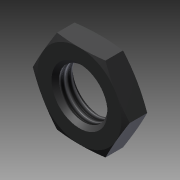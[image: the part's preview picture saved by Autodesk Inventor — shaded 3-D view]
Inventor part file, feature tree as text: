
AUTODESK INVENTOR PART (.ipt)
format: ipt  version: 2011 SP1 (Build 150282100, 282)  size: 116,224 bytes
history: native  units: mm
features: other x7, sketch x2, revolve x1, thread x1, extrude x1
ambient origin geometry x8: Origin, YZ Plane, XZ Plane, XY Plane, X Axis, Y Axis, Z Axis, Center Point
bodies: Solid1 (feature_tree)
feature tree (12):
  revolve  "Revolution1"  [1 undecoded]
  thread  "Thread1"  [1 undecoded]
  extrude  "Extrusion1"  [1 undecoded]
  other  "NUT_BUFFER_XY"
  other  "NUT_BUFFER_YZ"
  other  "NUT_BUFFER_ZX"
  other  "NUT_BUFFER_X"
  other  "NUT_BUFFER_Y"
  other  "NUT_BUFFER_Z"
  other  "NUT_BUFFER_Center"
  sketch  "Sketch_1"  dims[d0=360.0deg d1=1.917mm d2=0.0mm d3=3.0mm d4=0.0mm]
  sketch  "Sketch_2"
note: 3 required parameter values undecoded (feature->parameter linkage not recoverable at this tier; creation-order binding heuristic only, values carry confidence <= 0.55)